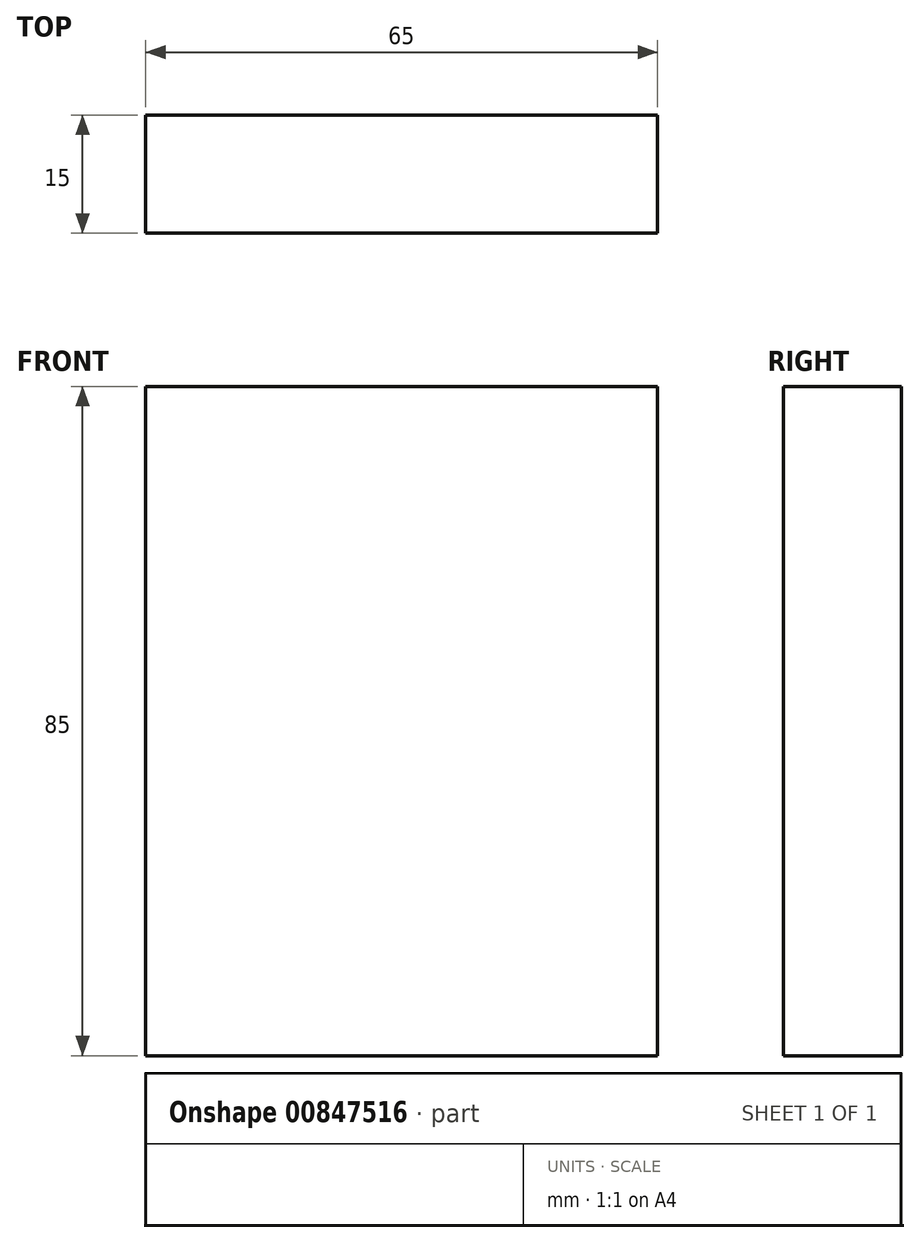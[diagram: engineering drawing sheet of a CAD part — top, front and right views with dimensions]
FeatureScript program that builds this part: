
annotation { "Feature Type Name" : "Feature", "Feature Type Description" : "" }
export const myFeature = defineFeature(function(context is Context, id is Id, definition is map)
    precondition{}
    {
        {
            var Q0;
            Q0=qCreatedBy(makeId("Front.planeOp"),FACE);
            var sketch = newSketch(context, id + "F0", { "sketchPlane" : qUnion([Q0])});
            skLineSegment(sketch, "E0.bottom", {"start": v(-32.15, 42.96) * mm, "end": v(32.85, 42.96) * mm});
            skLineSegment(sketch, "E0.top", {"start": v(-32.15, -42.04) * mm, "end": v(32.85, -42.04) * mm});
            skLineSegment(sketch, "E0.left", {"start": v(-32.15, 42.96) * mm, "end": v(-32.15, -42.04) * mm});
            skLineSegment(sketch, "E0.right", {"start": v(32.85, 42.96) * mm, "end": v(32.85, -42.04) * mm});
            skSolve(sketch);
        }
        {
            var Q0;
            Q0=makeQuery(id+"F0.imprint","IMPRINT",FACE,{"disambiguationData":[TD([[makeQuery(id+"F0.imprint","IMPRINT",EDGE,{"derivedFrom":sQuery(id+"F0.wireOp",EDGE,"E0.bottom")}),-1.0]])]});
            extrude(context, id + "F1", {"entities" : qUnion([Q0]), "depth" : 15 * mm, "offsetDistance" : 25 * mm});
        }
    });
